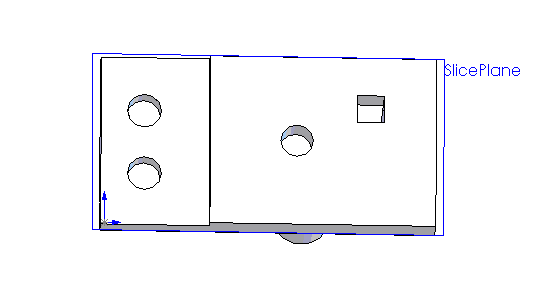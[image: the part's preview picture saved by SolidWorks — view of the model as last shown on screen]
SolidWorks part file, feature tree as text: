
SOLIDWORKS PART (.sldprt)
format: sldprt  version: not decoded by parser v0  size: 203,776 bytes
history: native  units: mm
features: sketch x6, cut_extrude x4, extrude x2, plane x1 (+11 scaffold rows collapsed)
feature tree (24):
  scaffold x11  (default folders/planes/origin — collapsed)
  sketch  "Sketch1"  dims[D1=50.8mm D2=97.79mm]
  extrude  "Extrude2"  Depth=9.525mm
  sketch  "Sketch3"  dims[D1=38.1mm D2=57.15mm D3=31.75mm]
  cut_extrude  "Cut-Extrude1"  Depth=3.175mm
  sketch  "Sketch4"  dims[c1.D3=9.9314mm c1.D4=9.9314mm c1.D7=9.525mm c1.D1=25.4mm c1.D2=12.7mm c1.D5=9.2964mm c2.D1=18.9992mm c2.D6=25.4mm c2.D8=25.4mm c2.D9=25.4mm c2.D10=~9.397593mm c2.D11=~9.20181mm c2.D12=~21.702567mm c2.D13=~4.541054mm]
  cut_extrude  "Cut-Extrude2"  [1 undecoded]
  sketch  "Sketch5"  dims[D1=9.525mm D2=25.4mm D3=25.4mm]
  cut_extrude  "Cut-Extrude3"  [1 undecoded]
  plane  "SlicePlane"  Offset=5.1054mm
  sketch  "Sketch6"
  extrude  "Extrude3"  Depth=12.7mm
  sketch  "Sketch7"
  cut_extrude  "Cut-Extrude4"  [1 undecoded]
decode coverage: 7 of 12 modeling features carry decoded parameters
note: ~ marks probable driven/reference dimensions
note: 3 parameter values undecoded
summary: no parameter record found for 3 features
note: suppression state not decoded; provenance and decode notes live in map.json
